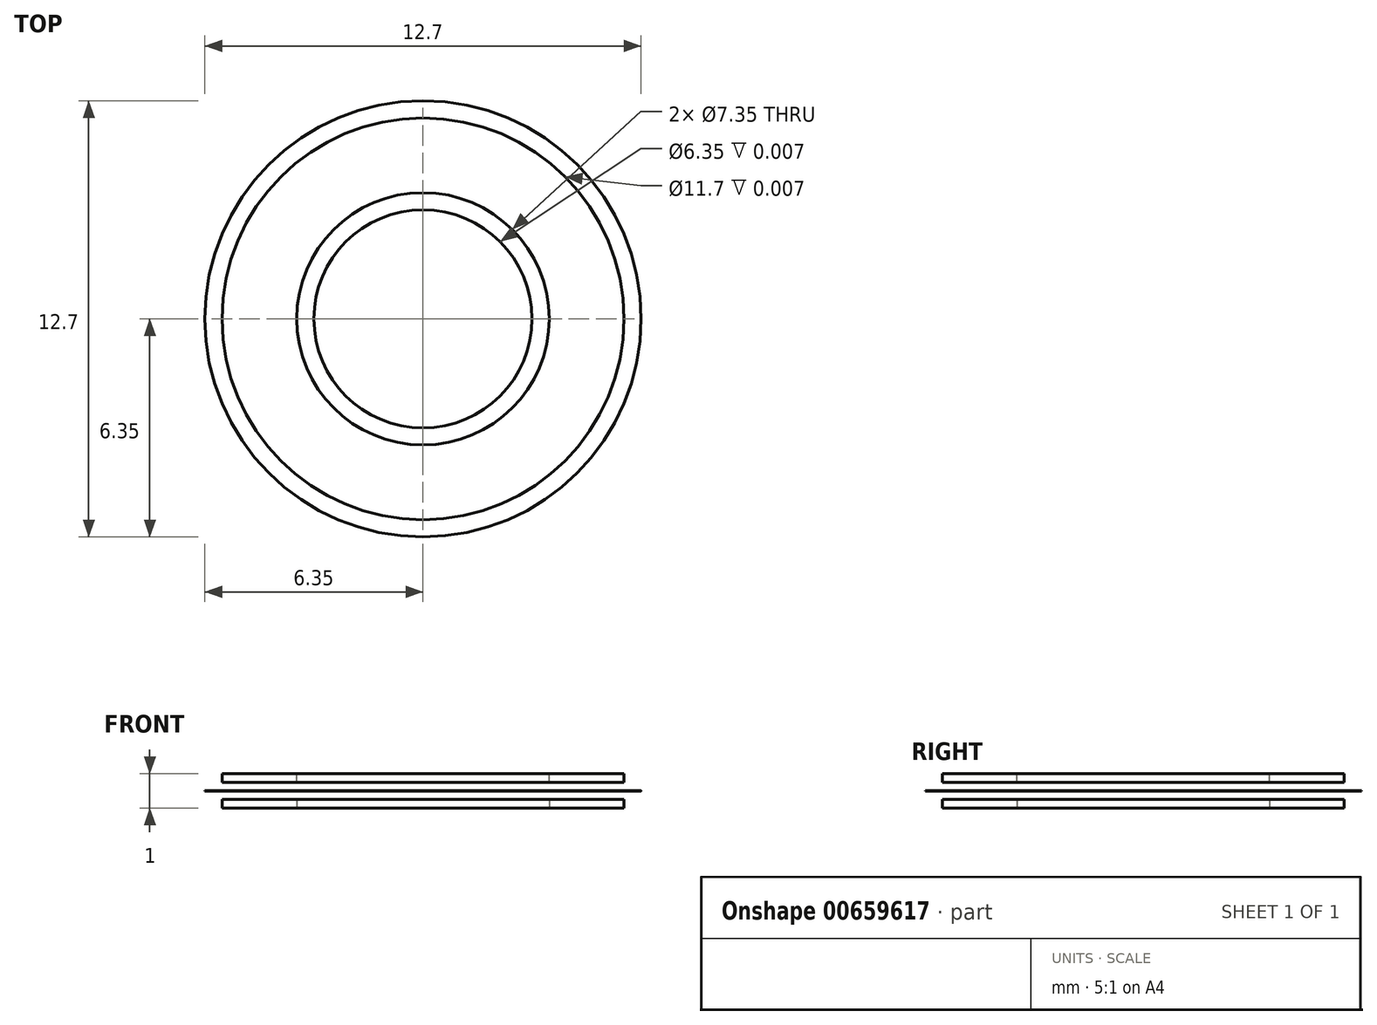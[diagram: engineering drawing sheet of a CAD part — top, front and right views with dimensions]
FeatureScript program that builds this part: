
annotation { "Feature Type Name" : "Feature", "Feature Type Description" : "" }
export const myFeature = defineFeature(function(context is Context, id is Id, definition is map)
    precondition{}
    {
        {
            var Q0;
            Q0=qCreatedBy(makeId("Top.planeOp"),FACE);
            var sketch = newSketch(context, id + "F0", { "sketchPlane" : qUnion([Q0])});
            skCircle(sketch, "E0", {"center": v(0, 0) * mm, "radius": 6.35 * mm});
            skCircle(sketch, "E1", {"center": v(0, 0) * mm, "radius": 3.18 * mm});
            skCircle(sketch, "E2", {"center": v(0, 0) * mm, "radius": 3.68 * mm});
            skCircle(sketch, "E3", {"center": v(0, 0) * mm, "radius": 5.85 * mm});
            skSolve(sketch);
        }
        {
            var Q0;
            Q0=makeQuery(id+"F0.imprint","IMPRINT",FACE,{"disambiguationData":[TD([[makeQuery(id+"F0.imprint","IMPRINT",EDGE,{"derivedFrom":sQuery(id+"F0.wireOp",EDGE,"E1")}),-1.0]])]});
            var Q1;
            Q1=makeQuery(id+"F0.imprint","IMPRINT",FACE,{"disambiguationData":[TD([[makeQuery(id+"F0.imprint","IMPRINT",EDGE,{"derivedFrom":sQuery(id+"F0.wireOp",EDGE,"E0")}),1.0]])]});
            extrude(context, id + "F1", {"entities" : qUnion([Q0, Q1]), "endBound" : BoundingType.SYMMETRIC, "depth" : 3 / 406.4 * mm, "offsetDistance" : 25 * mm});
        }
        {
            var Q0;
            Q0=makeQuery(id+"F1.opExtrude","CAP_FACE",FACE,{"disambiguationData":[OSD([sQuery(id+"F0.wireOp",EDGE,"E0"),sQuery(id+"F0.wireOp",EDGE,"E3")])],"isStart":false});
            cPlane(context, id + "F2", {"entities" : qUnion([Q0]), "cplaneType" : CPlaneType.OFFSET, "offset" : .5 * mm, "oppositeDirection" : true, "width" : 150 * mm, "height" : 150 * mm});
        }
        {
            var Q0;
            Q0=qCreatedBy(id+"F2.planeOp",FACE);
            var sketch = newSketch(context, id + "F3", { "sketchPlane" : qUnion([Q0])});
            skCircle(sketch, "E4.0", {"center": v(0, 0) * mm, "radius": 5.85 * mm});
            skCircle(sketch, "E5.0", {"center": v(0, 0) * mm, "radius": 3.68 * mm});
            skSolve(sketch);
        }
        {
            var Q0;
            Q0 = qSketchRegion(id + "F3", true);
            extrude(context, id + "F4", {"entities" : qUnion([Q0]), "depth" : .25 * mm, "offsetDistance" : 25 * mm});
        }
        {
            var Q0;
            Q0=makeQuery(id+"F4.opExtrude","SWEPT_BODY",BODY,{"disambiguationData":[OSD([sQuery(id+"F3.wireOp",EDGE,"E4.0"),sQuery(id+"F3.wireOp",EDGE,"E5.0")])]});
            var Q1;
            Q1=qCreatedBy(makeId("Top.planeOp"),FACE);
            mirror(context, id + "F5", {"entities" : qUnion([Q0]), "mirrorPlane" : qUnion([Q1])});
        }
    });
